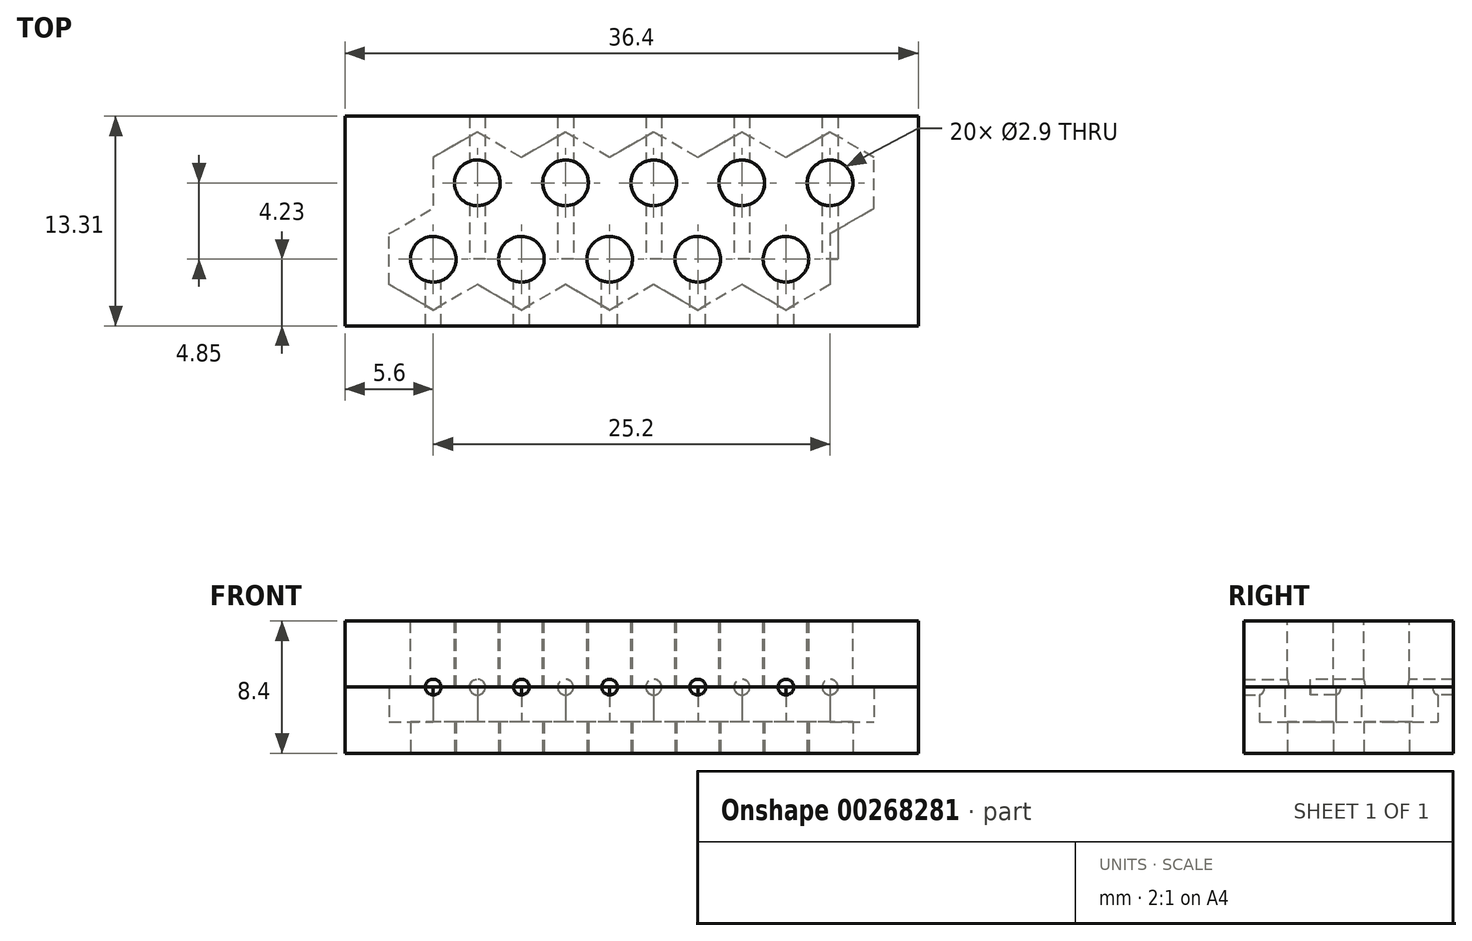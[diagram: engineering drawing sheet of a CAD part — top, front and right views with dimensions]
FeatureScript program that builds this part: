
annotation { "Feature Type Name" : "Feature", "Feature Type Description" : "" }
export const myFeature = defineFeature(function(context is Context, id is Id, definition is map)
    precondition{}
    {
        {
            assignVariable(context, id + "F0", {"name" : "NutThickness", "anyValue" : 2.2});
        }
        {
            assignVariable(context, id + "F1", {"name" : "BlockBase", "anyValue" : 2});
        }
        {
            var Q0;
            Q0=qCreatedBy(makeId("Top.planeOp"),FACE);
            var sketch = newSketch(context, id + "F2", { "sketchPlane" : qUnion([Q0])});
            skCircle(sketch, "E0", {"center": v(0, 0) * mm, "radius": 1.45 * mm});
            skCircle(sketch, "E1.cCircle", {"center": v(0, 0) * mm, "radius": 2.8 * mm, "construction": true});
            skLineSegment(sketch, "E1.0", {"start": v(-2.8, -1.62) * mm, "end": v(-2.8, 1.62) * mm});
            skLineSegment(sketch, "E1.1", {"start": v(-2.8, 1.62) * mm, "end": v(0, 3.23) * mm});
            skLineSegment(sketch, "E1.2", {"start": v(0, 3.23) * mm, "end": v(2.8, 1.62) * mm});
            skLineSegment(sketch, "E1.3", {"start": v(2.8, 1.62) * mm, "end": v(2.8, -1.62) * mm});
            skLineSegment(sketch, "E1.4", {"start": v(2.8, -1.62) * mm, "end": v(0, -3.23) * mm});
            skLineSegment(sketch, "E1.5", {"start": v(0, -3.23) * mm, "end": v(-2.8, -1.62) * mm});
            skPoint(sketch, "E1.0.midPoint", {"position": v(-2.8, 0) * mm});
            skLineSegment(sketch, "E2.MirrorCS", {"start": v(2.8, 1.62) * mm, "end": v(5.6, 3.23) * mm});
            skLineSegment(sketch, "E3.MirrorCS", {"start": v(5.6, 3.23) * mm, "end": v(5.6, 6.47) * mm});
            skLineSegment(sketch, "E4.MirrorCS", {"start": v(5.6, 6.47) * mm, "end": v(2.8, 8.08) * mm});
            skLineSegment(sketch, "E5.MirrorCS", {"start": v(2.8, 8.08) * mm, "end": v(0, 6.47) * mm});
            skLineSegment(sketch, "E6.MirrorCS", {"start": v(0, 6.47) * mm, "end": v(0, 3.23) * mm});
            skCircle(sketch, "E7.MirrorC", {"center": v(2.8, 4.85) * mm, "radius": 1.45 * mm});
            skLineSegment(sketch, "E8.1.0.0", {"start": v(8.4, 1.62) * mm, "end": v(11.2, 3.23) * mm});
            skLineSegment(sketch, "E8.1.0.1", {"start": v(11.2, 3.23) * mm, "end": v(11.2, 6.47) * mm});
            skLineSegment(sketch, "E8.1.0.2", {"start": v(11.2, 6.47) * mm, "end": v(8.4, 8.08) * mm});
            skLineSegment(sketch, "E8.1.0.3", {"start": v(8.4, 8.08) * mm, "end": v(5.6, 6.47) * mm});
            skLineSegment(sketch, "E8.1.0.4", {"start": v(5.6, 6.47) * mm, "end": v(5.6, 3.23) * mm});
            skCircle(sketch, "E8.1.0.5", {"center": v(8.4, 4.85) * mm, "radius": 1.45 * mm});
            skLineSegment(sketch, "E8.1.0.6", {"start": v(5.6, 3.23) * mm, "end": v(8.4, 1.62) * mm});
            skLineSegment(sketch, "E8.1.0.8", {"start": v(2.8, -1.62) * mm, "end": v(2.8, 1.62) * mm});
            skLineSegment(sketch, "E8.1.0.9", {"start": v(5.6, -3.23) * mm, "end": v(2.8, -1.62) * mm});
            skLineSegment(sketch, "E8.1.0.10", {"start": v(8.4, -1.62) * mm, "end": v(5.6, -3.23) * mm});
            skLineSegment(sketch, "E8.1.0.11", {"start": v(8.4, 1.62) * mm, "end": v(8.4, -1.62) * mm});
            skCircle(sketch, "E8.1.0.12", {"center": v(5.6, 0) * mm, "radius": 1.45 * mm});
            skLineSegment(sketch, "E8.2.0.0", {"start": v(14, 1.62) * mm, "end": v(16.8, 3.23) * mm});
            skLineSegment(sketch, "E8.2.0.1", {"start": v(16.8, 3.23) * mm, "end": v(16.8, 6.47) * mm});
            skLineSegment(sketch, "E8.2.0.2", {"start": v(16.8, 6.47) * mm, "end": v(14, 8.08) * mm});
            skLineSegment(sketch, "E8.2.0.3", {"start": v(14, 8.08) * mm, "end": v(11.2, 6.47) * mm});
            skLineSegment(sketch, "E8.2.0.4", {"start": v(11.2, 6.47) * mm, "end": v(11.2, 3.23) * mm});
            skCircle(sketch, "E8.2.0.5", {"center": v(14, 4.85) * mm, "radius": 1.45 * mm});
            skLineSegment(sketch, "E8.2.0.6", {"start": v(11.2, 3.23) * mm, "end": v(14, 1.62) * mm});
            skLineSegment(sketch, "E8.2.0.7", {"start": v(8.4, 1.62) * mm, "end": v(11.2, 3.23) * mm});
            skLineSegment(sketch, "E8.2.0.8", {"start": v(8.4, -1.62) * mm, "end": v(8.4, 1.62) * mm});
            skLineSegment(sketch, "E8.2.0.9", {"start": v(11.2, -3.23) * mm, "end": v(8.4, -1.62) * mm});
            skLineSegment(sketch, "E8.2.0.10", {"start": v(14, -1.62) * mm, "end": v(11.2, -3.23) * mm});
            skLineSegment(sketch, "E8.2.0.11", {"start": v(14, 1.62) * mm, "end": v(14, -1.62) * mm});
            skCircle(sketch, "E8.2.0.12", {"center": v(11.2, 0) * mm, "radius": 1.45 * mm});
            skLineSegment(sketch, "E8.3.0.0", {"start": v(19.6, 1.62) * mm, "end": v(22.4, 3.23) * mm});
            skLineSegment(sketch, "E8.3.0.1", {"start": v(22.4, 3.23) * mm, "end": v(22.4, 6.47) * mm});
            skLineSegment(sketch, "E8.3.0.2", {"start": v(22.4, 6.47) * mm, "end": v(19.6, 8.08) * mm});
            skLineSegment(sketch, "E8.3.0.3", {"start": v(19.6, 8.08) * mm, "end": v(16.8, 6.47) * mm});
            skLineSegment(sketch, "E8.3.0.4", {"start": v(16.8, 6.47) * mm, "end": v(16.8, 3.23) * mm});
            skCircle(sketch, "E8.3.0.5", {"center": v(19.6, 4.85) * mm, "radius": 1.45 * mm});
            skLineSegment(sketch, "E8.3.0.6", {"start": v(16.8, 3.23) * mm, "end": v(19.6, 1.62) * mm});
            skLineSegment(sketch, "E8.3.0.7", {"start": v(14, 1.62) * mm, "end": v(16.8, 3.23) * mm});
            skLineSegment(sketch, "E8.3.0.8", {"start": v(14, -1.62) * mm, "end": v(14, 1.62) * mm});
            skLineSegment(sketch, "E8.3.0.9", {"start": v(16.8, -3.23) * mm, "end": v(14, -1.62) * mm});
            skLineSegment(sketch, "E8.3.0.10", {"start": v(19.6, -1.62) * mm, "end": v(16.8, -3.23) * mm});
            skLineSegment(sketch, "E8.3.0.11", {"start": v(19.6, 1.62) * mm, "end": v(19.6, -1.62) * mm});
            skCircle(sketch, "E8.3.0.12", {"center": v(16.8, 0) * mm, "radius": 1.45 * mm});
            skLineSegment(sketch, "E8.4.0.0", {"start": v(25.2, 1.62) * mm, "end": v(28, 3.23) * mm});
            skLineSegment(sketch, "E8.4.0.1", {"start": v(28, 3.23) * mm, "end": v(28, 6.47) * mm});
            skLineSegment(sketch, "E8.4.0.2", {"start": v(28, 6.47) * mm, "end": v(25.2, 8.08) * mm});
            skLineSegment(sketch, "E8.4.0.3", {"start": v(25.2, 8.08) * mm, "end": v(22.4, 6.47) * mm});
            skLineSegment(sketch, "E8.4.0.4", {"start": v(22.4, 6.47) * mm, "end": v(22.4, 3.23) * mm});
            skCircle(sketch, "E8.4.0.5", {"center": v(25.2, 4.85) * mm, "radius": 1.45 * mm});
            skLineSegment(sketch, "E8.4.0.6", {"start": v(22.4, 3.23) * mm, "end": v(25.2, 1.62) * mm});
            skLineSegment(sketch, "E8.4.0.7", {"start": v(19.6, 1.62) * mm, "end": v(22.4, 3.23) * mm});
            skLineSegment(sketch, "E8.4.0.8", {"start": v(19.6, -1.62) * mm, "end": v(19.6, 1.62) * mm});
            skLineSegment(sketch, "E8.4.0.9", {"start": v(22.4, -3.23) * mm, "end": v(19.6, -1.62) * mm});
            skLineSegment(sketch, "E8.4.0.10", {"start": v(25.2, -1.62) * mm, "end": v(22.4, -3.23) * mm});
            skLineSegment(sketch, "E8.4.0.11", {"start": v(25.2, 1.62) * mm, "end": v(25.2, -1.62) * mm});
            skCircle(sketch, "E8.4.0.12", {"center": v(22.4, 0) * mm, "radius": 1.45 * mm});
            skLineSegment(sketch, "E8.direction1", {"start": v(2.8, 1.62) * mm, "end": v(8.4, 1.62) * mm, "construction": true});
            skLineSegment(sketch, "E9.bottom", {"start": v(-5.6, -4.23) * mm, "end": v(30.8, -4.23) * mm});
            skLineSegment(sketch, "E9.top", {"start": v(-5.6, 9.08) * mm, "end": v(30.8, 9.08) * mm});
            skLineSegment(sketch, "E9.left", {"start": v(-5.6, -4.23) * mm, "end": v(-5.6, 9.08) * mm});
            skLineSegment(sketch, "E9.right", {"start": v(30.8, -4.23) * mm, "end": v(30.8, 9.08) * mm});
            skLineSegment(sketch, "E10", {"start": v(0, -3.23) * mm, "end": v(0, -4.23) * mm, "construction": true});
            skSolve(sketch);
        }
        {
            var Q0;
            Q0=makeQuery(id+"F2.imprint","IMPRINT",FACE,{"disambiguationData":[TD([[makeQuery(id+"F2.imprint","IMPRINT",EDGE,{"derivedFrom":sQuery(id+"F2.wireOp",EDGE,"E1.0")}),1.0]])]});
            var Q1;
            Q1=makeQuery(id+"F2.imprint","IMPRINT",FACE,{"disambiguationData":[TD([[makeQuery(id+"F2.imprint","IMPRINT",EDGE,{"derivedFrom":sQuery(id+"F2.wireOp",EDGE,"E8.4.0.6")}),-1.0]])]});
            var Q2;
            Q2=makeQuery(id+"F2.imprint","IMPRINT",FACE,{"disambiguationData":[TD([[makeQuery(id+"F2.imprint","IMPRINT",EDGE,{"derivedFrom":sQuery(id+"F2.wireOp",EDGE,"E8.4.0.0")}),1.0]])]});
            var Q3;
            Q3=makeQuery(id+"F2.imprint","IMPRINT",FACE,{"disambiguationData":[TD([[makeQuery(id+"F2.imprint","IMPRINT",EDGE,{"derivedFrom":sQuery(id+"F2.wireOp",EDGE,"E8.3.0.2")}),1.0]])]});
            var Q4;
            Q4=makeQuery(id+"F2.imprint","IMPRINT",FACE,{"disambiguationData":[TD([[makeQuery(id+"F2.imprint","IMPRINT",EDGE,{"derivedFrom":sQuery(id+"F2.wireOp",EDGE,"E1.2")}),1.0]])]});
            var Q5;
            Q5=makeQuery(id+"F2.imprint","IMPRINT",FACE,{"disambiguationData":[TD([[makeQuery(id+"F2.imprint","IMPRINT",EDGE,{"derivedFrom":sQuery(id+"F2.wireOp",EDGE,"E0")}),-1.0]])]});
            var Q6;
            Q6=makeQuery(id+"F2.imprint","IMPRINT",FACE,{"disambiguationData":[TD([[makeQuery(id+"F2.imprint","IMPRINT",EDGE,{"derivedFrom":sQuery(id+"F2.wireOp",EDGE,"E8.1.0.6")}),-1.0]])]});
            var Q7;
            Q7=makeQuery(id+"F2.imprint","IMPRINT",FACE,{"disambiguationData":[TD([[makeQuery(id+"F2.imprint","IMPRINT",EDGE,{"derivedFrom":sQuery(id+"F2.wireOp",EDGE,"E8.1.0.2")}),1.0]])]});
            var Q8;
            Q8=makeQuery(id+"F2.imprint","IMPRINT",FACE,{"disambiguationData":[TD([[makeQuery(id+"F2.imprint","IMPRINT",EDGE,{"derivedFrom":sQuery(id+"F2.wireOp",EDGE,"E8.2.0.6")}),-1.0]])]});
            var Q9;
            Q9=makeQuery(id+"F2.imprint","IMPRINT",FACE,{"disambiguationData":[TD([[makeQuery(id+"F2.imprint","IMPRINT",EDGE,{"derivedFrom":sQuery(id+"F2.wireOp",EDGE,"E8.2.0.2")}),1.0]])]});
            var Q10;
            Q10=makeQuery(id+"F2.imprint","IMPRINT",FACE,{"disambiguationData":[TD([[makeQuery(id+"F2.imprint","IMPRINT",EDGE,{"derivedFrom":sQuery(id+"F2.wireOp",EDGE,"E8.3.0.6")}),-1.0]])]});
            extrude(context, id + "F3", {"entities" : qUnion([Q0, Q1, Q2, Q3, Q4, Q5, Q6, Q7, Q8, Q9, Q10]), "depth" : (getVariable(context, 'BlockBase') + getVariable(context, 'NutThickness')) * mm, "offsetDistance" : 25 * mm});
        }
        {
            var Q0;
            Q0=makeQuery(id+"F3.opExtrude","SWEPT_BODY",BODY,{"disambiguationData":[OSD([sQuery(id+"F2.wireOp",EDGE,"E0"),sQuery(id+"F2.wireOp",EDGE,"E7.MirrorC"),sQuery(id+"F2.wireOp",EDGE,"E8.1.0.5"),sQuery(id+"F2.wireOp",EDGE,"E8.1.0.12"),sQuery(id+"F2.wireOp",EDGE,"E8.2.0.5"),sQuery(id+"F2.wireOp",EDGE,"E8.2.0.12"),sQuery(id+"F2.wireOp",EDGE,"E8.3.0.5"),sQuery(id+"F2.wireOp",EDGE,"E8.3.0.12"),sQuery(id+"F2.wireOp",EDGE,"E8.4.0.5"),sQuery(id+"F2.wireOp",EDGE,"E8.4.0.12"),sQuery(id+"F2.wireOp",EDGE,"E9.bottom"),sQuery(id+"F2.wireOp",EDGE,"E9.top"),sQuery(id+"F2.wireOp",EDGE,"E9.left"),sQuery(id+"F2.wireOp",EDGE,"E9.right")])]});
            var Q1;
            Q1=makeQuery(id+"F3.opExtrude","CAP_FACE",FACE,{"disambiguationData":[OSD([sQuery(id+"F2.wireOp",EDGE,"E0"),sQuery(id+"F2.wireOp",EDGE,"E7.MirrorC"),sQuery(id+"F2.wireOp",EDGE,"E8.1.0.5"),sQuery(id+"F2.wireOp",EDGE,"E8.1.0.12"),sQuery(id+"F2.wireOp",EDGE,"E8.2.0.5"),sQuery(id+"F2.wireOp",EDGE,"E8.2.0.12"),sQuery(id+"F2.wireOp",EDGE,"E8.3.0.5"),sQuery(id+"F2.wireOp",EDGE,"E8.3.0.12"),sQuery(id+"F2.wireOp",EDGE,"E8.4.0.5"),sQuery(id+"F2.wireOp",EDGE,"E8.4.0.12"),sQuery(id+"F2.wireOp",EDGE,"E9.bottom"),sQuery(id+"F2.wireOp",EDGE,"E9.top"),sQuery(id+"F2.wireOp",EDGE,"E9.left"),sQuery(id+"F2.wireOp",EDGE,"E9.right")])],"isStart":false});
            mirror(context, id + "F4", {"entities" : qUnion([Q0]), "mirrorPlane" : qUnion([Q1])});
        }
        {
            var Q0;
            Q0=makeQuery(id+"F2.imprint","IMPRINT",FACE,{"disambiguationData":[TD([[makeQuery(id+"F2.imprint","IMPRINT",EDGE,{"derivedFrom":sQuery(id+"F2.wireOp",EDGE,"E0")}),-1.0]])]});
            var Q1;
            Q1=makeQuery(id+"F2.imprint","IMPRINT",FACE,{"disambiguationData":[TD([[makeQuery(id+"F2.imprint","IMPRINT",EDGE,{"derivedFrom":sQuery(id+"F2.wireOp",EDGE,"E1.2")}),1.0]])]});
            var Q2;
            Q2=makeQuery(id+"F2.imprint","IMPRINT",FACE,{"disambiguationData":[TD([[makeQuery(id+"F2.imprint","IMPRINT",EDGE,{"derivedFrom":sQuery(id+"F2.wireOp",EDGE,"E8.1.0.6")}),-1.0]])]});
            var Q3;
            Q3=makeQuery(id+"F2.imprint","IMPRINT",FACE,{"disambiguationData":[TD([[makeQuery(id+"F2.imprint","IMPRINT",EDGE,{"derivedFrom":sQuery(id+"F2.wireOp",EDGE,"E8.1.0.2")}),1.0]])]});
            var Q4;
            Q4=makeQuery(id+"F2.imprint","IMPRINT",FACE,{"disambiguationData":[TD([[makeQuery(id+"F2.imprint","IMPRINT",EDGE,{"derivedFrom":sQuery(id+"F2.wireOp",EDGE,"E8.2.0.6")}),-1.0]])]});
            var Q5;
            Q5=makeQuery(id+"F2.imprint","IMPRINT",FACE,{"disambiguationData":[TD([[makeQuery(id+"F2.imprint","IMPRINT",EDGE,{"derivedFrom":sQuery(id+"F2.wireOp",EDGE,"E8.2.0.2")}),1.0]])]});
            var Q6;
            Q6=makeQuery(id+"F2.imprint","IMPRINT",FACE,{"disambiguationData":[TD([[makeQuery(id+"F2.imprint","IMPRINT",EDGE,{"derivedFrom":sQuery(id+"F2.wireOp",EDGE,"E8.3.0.6")}),-1.0]])]});
            var Q7;
            Q7=makeQuery(id+"F2.imprint","IMPRINT",FACE,{"disambiguationData":[TD([[makeQuery(id+"F2.imprint","IMPRINT",EDGE,{"derivedFrom":sQuery(id+"F2.wireOp",EDGE,"E8.3.0.2")}),1.0]])]});
            var Q8;
            Q8=makeQuery(id+"F2.imprint","IMPRINT",FACE,{"disambiguationData":[TD([[makeQuery(id+"F2.imprint","IMPRINT",EDGE,{"derivedFrom":sQuery(id+"F2.wireOp",EDGE,"E8.4.0.6")}),-1.0]])]});
            var Q9;
            Q9=makeQuery(id+"F2.imprint","IMPRINT",FACE,{"disambiguationData":[TD([[makeQuery(id+"F2.imprint","IMPRINT",EDGE,{"derivedFrom":sQuery(id+"F2.wireOp",EDGE,"E8.4.0.0")}),1.0]])]});
            extrude(context, id + "F5", {"entities" : qUnion([Q0, Q1, Q2, Q3, Q4, Q5, Q6, Q7, Q8, Q9]), "operationType" : NewBodyOperationType.REMOVE, "depth" : (getVariable(context, 'BlockBase') + getVariable(context, 'NutThickness')) * mm, "offsetDistance" : 25 * mm, "hasSecondDirection" : true, "secondDirectionOppositeDirection" : false, "secondDirectionDepth" : (getVariable(context, 'BlockBase')) * mm});
        }
        {
            var Q0;
            Q0=qCreatedBy(makeId("Front.planeOp"),FACE);
            var sketch = newSketch(context, id + "F6", { "sketchPlane" : qUnion([Q0])});
            skLineSegment(sketch, "E11", {"start": v(0, 0) * mm, "end": v(0, 4.2) * mm, "construction": true});
            skCircle(sketch, "E12", {"center": v(0, 4.2) * mm, "radius": 0.5 * mm});
            skCircle(sketch, "E13.1.0.0", {"center": v(2.8, 4.2) * mm, "radius": 0.5 * mm});
            skCircle(sketch, "E13.2.0.0", {"center": v(5.6, 4.2) * mm, "radius": 0.5 * mm});
            skCircle(sketch, "E13.3.0.0", {"center": v(8.4, 4.2) * mm, "radius": 0.5 * mm});
            skCircle(sketch, "E13.4.0.0", {"center": v(11.2, 4.2) * mm, "radius": 0.5 * mm});
            skCircle(sketch, "E13.5.0.0", {"center": v(14, 4.2) * mm, "radius": 0.5 * mm});
            skCircle(sketch, "E13.6.0.0", {"center": v(16.8, 4.2) * mm, "radius": 0.5 * mm});
            skCircle(sketch, "E13.7.0.0", {"center": v(19.6, 4.2) * mm, "radius": 0.5 * mm});
            skCircle(sketch, "E13.8.0.0", {"center": v(22.4, 4.2) * mm, "radius": 0.5 * mm});
            skLineSegment(sketch, "E13.direction1", {"start": v(0, 4.2) * mm, "end": v(2.8, 4.2) * mm, "construction": true});
            skCircle(sketch, "E14.0.9.0", {"center": v(25.2, 4.2) * mm, "radius": 0.5 * mm});
            skSolve(sketch);
        }
        {
            var Q0;
            Q0=makeQuery(id+"F6.imprint","IMPRINT",FACE,{"disambiguationData":[TD([[makeQuery(id+"F6.imprint","IMPRINT",EDGE,{"derivedFrom":sQuery(id+"F6.wireOp",EDGE,"E12")}),1.0]])]});
            var Q1;
            Q1=makeQuery(id+"F6.imprint","IMPRINT",FACE,{"disambiguationData":[TD([[makeQuery(id+"F6.imprint","IMPRINT",EDGE,{"derivedFrom":sQuery(id+"F6.wireOp",EDGE,"E13.2.0.0")}),1.0]])]});
            var Q2;
            Q2=makeQuery(id+"F6.imprint","IMPRINT",FACE,{"disambiguationData":[TD([[makeQuery(id+"F6.imprint","IMPRINT",EDGE,{"derivedFrom":sQuery(id+"F6.wireOp",EDGE,"E13.4.0.0")}),1.0]])]});
            var Q3;
            Q3=makeQuery(id+"F6.imprint","IMPRINT",FACE,{"disambiguationData":[TD([[makeQuery(id+"F6.imprint","IMPRINT",EDGE,{"derivedFrom":sQuery(id+"F6.wireOp",EDGE,"E13.6.0.0")}),1.0]])]});
            var Q4;
            Q4=makeQuery(id+"F6.imprint","IMPRINT",FACE,{"disambiguationData":[TD([[makeQuery(id+"F6.imprint","IMPRINT",EDGE,{"derivedFrom":sQuery(id+"F6.wireOp",EDGE,"E13.8.0.0")}),1.0]])]});
            var Q5;
            Q5=makeQuery(id+"F3.opExtrude","SWEPT_FACE",FACE,{"disambiguationData":[OSD([sQuery(id+"F2.wireOp",EDGE,"E9.bottom")])]});
            extrude(context, id + "F7", {"entities" : qUnion([Q0, Q1, Q2, Q3, Q4]), "operationType" : NewBodyOperationType.REMOVE, "endBound" : BoundingType.UP_TO_SURFACE, "depth" : 25 * mm, "endBoundEntityFace" : qUnion([Q5]), "offsetDistance" : 25 * mm});
        }
        {
            var Q0;
            Q0=makeQuery(id+"F6.imprint","IMPRINT",FACE,{"disambiguationData":[TD([[makeQuery(id+"F6.imprint","IMPRINT",EDGE,{"derivedFrom":sQuery(id+"F6.wireOp",EDGE,"E13.1.0.0")}),1.0]])]});
            var Q1;
            Q1=makeQuery(id+"F6.imprint","IMPRINT",FACE,{"disambiguationData":[TD([[makeQuery(id+"F6.imprint","IMPRINT",EDGE,{"derivedFrom":sQuery(id+"F6.wireOp",EDGE,"E13.3.0.0")}),1.0]])]});
            var Q2;
            Q2=makeQuery(id+"F6.imprint","IMPRINT",FACE,{"disambiguationData":[TD([[makeQuery(id+"F6.imprint","IMPRINT",EDGE,{"derivedFrom":sQuery(id+"F6.wireOp",EDGE,"E13.5.0.0")}),1.0]])]});
            var Q3;
            Q3=makeQuery(id+"F6.imprint","IMPRINT",FACE,{"disambiguationData":[TD([[makeQuery(id+"F6.imprint","IMPRINT",EDGE,{"derivedFrom":sQuery(id+"F6.wireOp",EDGE,"E13.7.0.0")}),1.0]])]});
            var Q4;
            Q4=makeQuery(id+"F6.imprint","IMPRINT",FACE,{"disambiguationData":[TD([[makeQuery(id+"F6.imprint","IMPRINT",EDGE,{"derivedFrom":sQuery(id+"F6.wireOp",EDGE,"E14.0.9.0")}),1.0]])]});
            var Q5;
            Q5=makeQuery(id+"F3.opExtrude","SWEPT_FACE",FACE,{"disambiguationData":[OSD([sQuery(id+"F2.wireOp",EDGE,"E9.top")])]});
            extrude(context, id + "F8", {"entities" : qUnion([Q0, Q1, Q2, Q3, Q4]), "operationType" : NewBodyOperationType.REMOVE, "endBound" : BoundingType.UP_TO_SURFACE, "oppositeDirection" : true, "depth" : 25 * mm, "endBoundEntityFace" : qUnion([Q5]), "offsetDistance" : 25 * mm});
        }
    });
